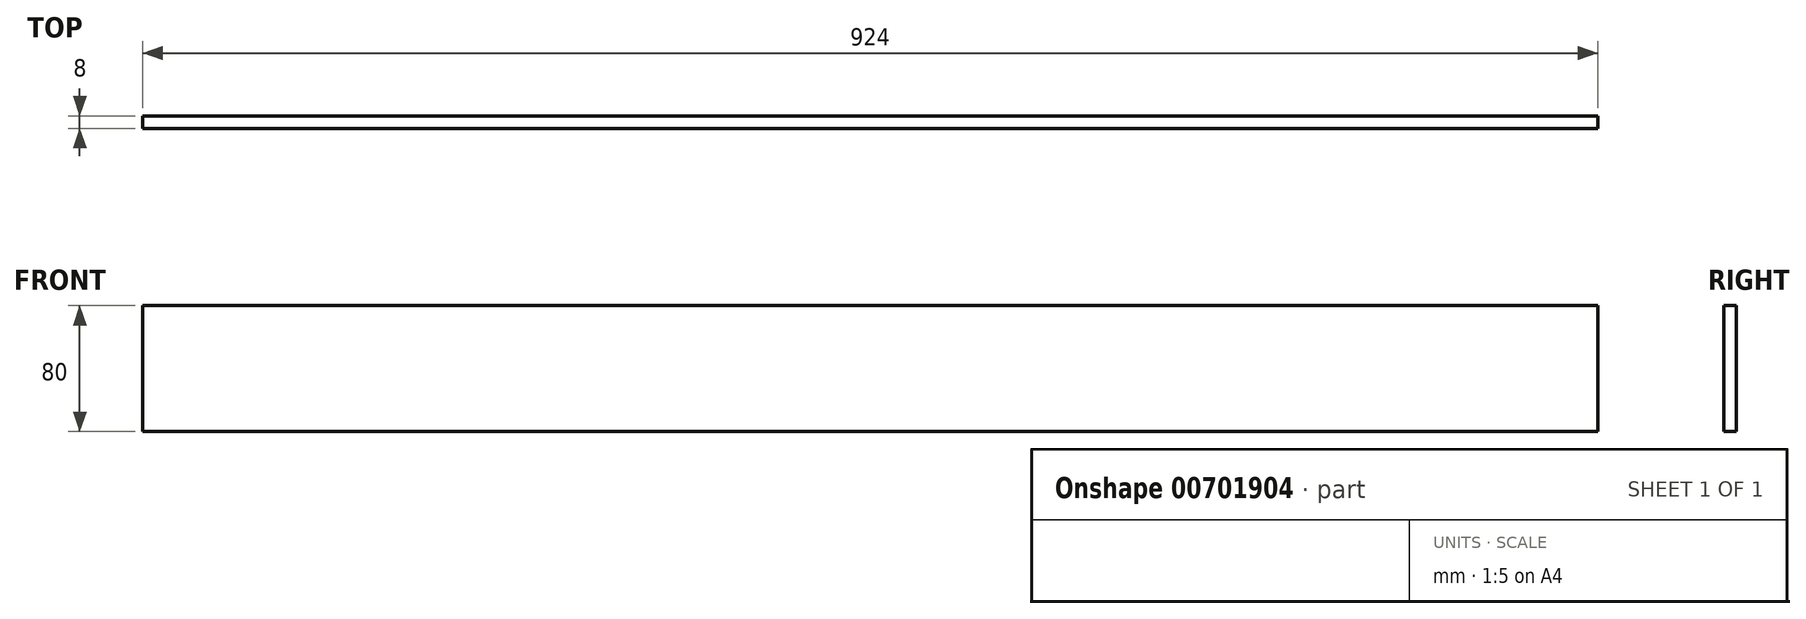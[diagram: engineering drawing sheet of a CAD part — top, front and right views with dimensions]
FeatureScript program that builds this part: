
annotation { "Feature Type Name" : "Feature", "Feature Type Description" : "" }
export const myFeature = defineFeature(function(context is Context, id is Id, definition is map)
    precondition{}
    {
        {
            var Q0;
            Q0=qCreatedBy(makeId("Front.planeOp"),FACE);
            var sketch = newSketch(context, id + "F0", { "sketchPlane" : qUnion([Q0])});
            skLineSegment(sketch, "E0.bottom", {"start": v(0, 0) * mm, "end": v(924, 0) * mm});
            skLineSegment(sketch, "E0.top", {"start": v(0, 80) * mm, "end": v(924, 80) * mm});
            skLineSegment(sketch, "E0.left", {"start": v(0, 0) * mm, "end": v(0, 80) * mm});
            skLineSegment(sketch, "E0.right", {"start": v(924, 0) * mm, "end": v(924, 80) * mm});
            skSolve(sketch);
        }
        {
            var Q0;
            Q0=makeQuery(id+"F0.imprint","IMPRINT",FACE,{"disambiguationData":[TD([[makeQuery(id+"F0.imprint","IMPRINT",EDGE,{"derivedFrom":sQuery(id+"F0.wireOp",EDGE,"E0.bottom")}),1.0]])]});
            extrude(context, id + "F1", {"entities" : qUnion([Q0]), "depth" : 8 * mm, "offsetDistance" : 25 * mm});
        }
    });
